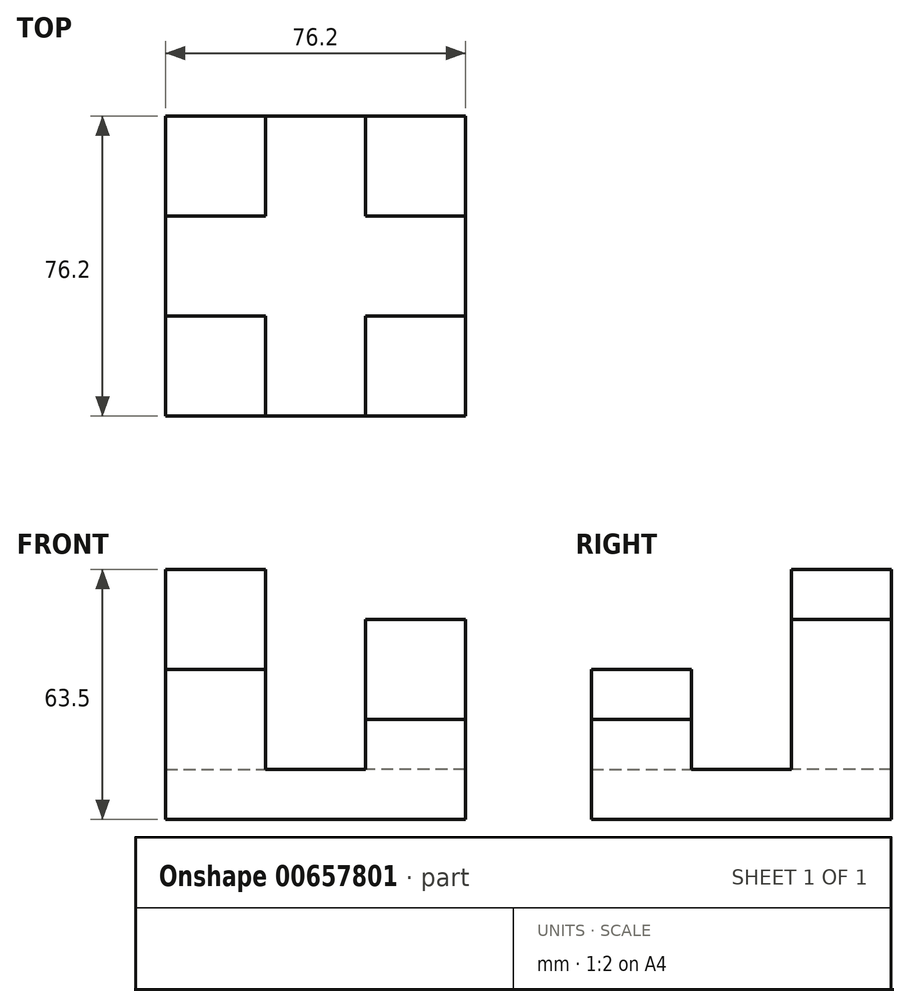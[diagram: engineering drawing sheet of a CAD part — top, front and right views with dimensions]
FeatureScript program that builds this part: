
annotation { "Feature Type Name" : "Feature", "Feature Type Description" : "" }
export const myFeature = defineFeature(function(context is Context, id is Id, definition is map)
    precondition{}
    {
        {
            var Q0;
            Q0=qCreatedBy(makeId("Top.planeOp"),FACE);
            var sketch = newSketch(context, id + "F0", { "sketchPlane" : qUnion([Q0])});
            skLineSegment(sketch, "E0.bottom", {"start": v(26.34, -19.1) * mm, "end": v(102.54, -19.1) * mm});
            skLineSegment(sketch, "E0.top", {"start": v(26.34, -95.3) * mm, "end": v(102.54, -95.3) * mm});
            skLineSegment(sketch, "E0.left", {"start": v(26.34, -19.1) * mm, "end": v(26.34, -95.3) * mm});
            skLineSegment(sketch, "E0.right", {"start": v(102.54, -19.1) * mm, "end": v(102.54, -95.3) * mm});
            skSolve(sketch);
        }
        {
            var Q0;
            Q0 = qSketchRegion(id + "F0", true);
            extrude(context, id + "F1", {"entities" : qUnion([Q0]), "depth" : 12.7 * mm, "offsetDistance" : 25.4 * mm});
        }
        {
            var Q0;
            Q0=makeQuery(id+"F1.opExtrude","CAP_FACE",FACE,{"disambiguationData":[OSD([sQuery(id+"F0.wireOp",EDGE,"E0.bottom"),sQuery(id+"F0.wireOp",EDGE,"E0.top"),sQuery(id+"F0.wireOp",EDGE,"E0.left"),sQuery(id+"F0.wireOp",EDGE,"E0.right")])],"isStart":false});
            var sketch = newSketch(context, id + "F2", { "sketchPlane" : qUnion([Q0])});
            skLineSegment(sketch, "E1.bottom", {"start": v(26.34, -95.3) * mm, "end": v(51.74, -95.3) * mm});
            skLineSegment(sketch, "E1.top", {"start": v(26.34, -69.9) * mm, "end": v(51.74, -69.9) * mm});
            skLineSegment(sketch, "E1.left", {"start": v(26.34, -95.3) * mm, "end": v(26.34, -69.9) * mm});
            skLineSegment(sketch, "E1.right", {"start": v(51.74, -95.3) * mm, "end": v(51.74, -69.9) * mm});
            skSolve(sketch);
        }
        {
            var Q0;
            Q0 = qSketchRegion(id + "F2", true);
            extrude(context, id + "F3", {"entities" : qUnion([Q0]), "operationType" : NewBodyOperationType.ADD, "depth" : 25.4 * mm, "offsetDistance" : 25.4 * mm});
        }
        {
            var Q0;
            Q0=makeQuery(id+"F1.opExtrude","CAP_FACE",FACE,{"disambiguationData":[OSD([sQuery(id+"F0.wireOp",EDGE,"E0.bottom"),sQuery(id+"F0.wireOp",EDGE,"E0.top"),sQuery(id+"F0.wireOp",EDGE,"E0.left"),sQuery(id+"F0.wireOp",EDGE,"E0.right")])],"isStart":false});
            var sketch = newSketch(context, id + "F4", { "sketchPlane" : qUnion([Q0])});
            skLineSegment(sketch, "E2.bottom", {"start": v(102.54, -95.3) * mm, "end": v(77.14, -95.3) * mm});
            skLineSegment(sketch, "E2.top", {"start": v(102.54, -69.9) * mm, "end": v(77.14, -69.9) * mm});
            skLineSegment(sketch, "E2.left", {"start": v(102.54, -95.3) * mm, "end": v(102.54, -69.9) * mm});
            skLineSegment(sketch, "E2.right", {"start": v(77.14, -95.3) * mm, "end": v(77.14, -69.9) * mm});
            skSolve(sketch);
        }
        {
            var Q0;
            Q0=makeQuery(id+"F4.imprint","IMPRINT",FACE,{"disambiguationData":[TD([[makeQuery(id+"F4.imprint","IMPRINT",EDGE,{"derivedFrom":sQuery(id+"F4.wireOp",EDGE,"E2.bottom")}),1.0]])]});
            extrude(context, id + "F5", {"entities" : qUnion([Q0]), "operationType" : NewBodyOperationType.ADD, "depth" : 12.7 * mm, "offsetDistance" : 25.4 * mm});
        }
        {
            var Q0;
            Q0=makeQuery(id+"F1.opExtrude","CAP_FACE",FACE,{"disambiguationData":[OSD([sQuery(id+"F0.wireOp",EDGE,"E0.bottom"),sQuery(id+"F0.wireOp",EDGE,"E0.top"),sQuery(id+"F0.wireOp",EDGE,"E0.left"),sQuery(id+"F0.wireOp",EDGE,"E0.right")])],"isStart":false});
            var sketch = newSketch(context, id + "F6", { "sketchPlane" : qUnion([Q0])});
            skLineSegment(sketch, "E3.bottom", {"start": v(102.54, -19.1) * mm, "end": v(77.14, -19.1) * mm});
            skLineSegment(sketch, "E3.top", {"start": v(102.54, -44.5) * mm, "end": v(77.14, -44.5) * mm});
            skLineSegment(sketch, "E3.left", {"start": v(102.54, -19.1) * mm, "end": v(102.54, -44.5) * mm});
            skLineSegment(sketch, "E3.right", {"start": v(77.14, -19.1) * mm, "end": v(77.14, -44.5) * mm});
            skSolve(sketch);
        }
        {
            var Q0;
            Q0 = qSketchRegion(id + "F6", true);
            extrude(context, id + "F7", {"entities" : qUnion([Q0]), "operationType" : NewBodyOperationType.ADD, "depth" : 38.1 * mm, "offsetDistance" : 25.4 * mm});
        }
        {
            var Q0;
            Q0=makeQuery(id+"F1.opExtrude","CAP_FACE",FACE,{"disambiguationData":[OSD([sQuery(id+"F0.wireOp",EDGE,"E0.bottom"),sQuery(id+"F0.wireOp",EDGE,"E0.top"),sQuery(id+"F0.wireOp",EDGE,"E0.left"),sQuery(id+"F0.wireOp",EDGE,"E0.right")])],"isStart":false});
            var sketch = newSketch(context, id + "F8", { "sketchPlane" : qUnion([Q0])});
            skLineSegment(sketch, "E4.bottom", {"start": v(26.34, -19.1) * mm, "end": v(51.74, -19.1) * mm});
            skLineSegment(sketch, "E4.top", {"start": v(26.34, -44.5) * mm, "end": v(51.74, -44.5) * mm});
            skLineSegment(sketch, "E4.left", {"start": v(26.34, -19.1) * mm, "end": v(26.34, -44.5) * mm});
            skLineSegment(sketch, "E4.right", {"start": v(51.74, -19.1) * mm, "end": v(51.74, -44.5) * mm});
            skSolve(sketch);
        }
        {
            var Q0;
            Q0 = qSketchRegion(id + "F8", true);
            extrude(context, id + "F9", {"entities" : qUnion([Q0]), "operationType" : NewBodyOperationType.ADD, "depth" : 50.8 * mm, "offsetDistance" : 25.4 * mm});
        }
    });
